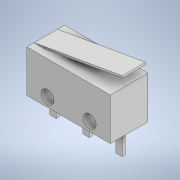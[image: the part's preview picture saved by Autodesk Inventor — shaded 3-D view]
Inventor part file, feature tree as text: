
AUTODESK INVENTOR PART (.ipt)
format: ipt  version: 2021 (Build 250183000, 183)  size: 138,752 bytes
history: native  units: mm
features: extrude x3, sketch x3
ambient origin geometry x8: Origin, YZ Plane, XZ Plane, XY Plane, X Axis, Y Axis, Z Axis, Center Point
bodies: Solid1 (feature_tree)
feature tree (6):
  extrude  "Extrusion1"  Depth=6.5mm
  extrude  "Extrusion2"  Depth=6.5mm
  extrude  "Extrusion3"  Depth=0.45mm
  sketch  "Sketch1"  dims[d0=12.85mm d1=6.5mm]
  sketch  "Sketch2"  dims[d2=1.4mm d3=6.5mm]
  sketch  "Sketch3"  dims[d4=3.25mm d5=2.0mm d6=5.8mm d7=0.0mm d9=0.3mm d10=1.745329mm d11=13.8mm d12=3.6mm d13=0.0mm d14=3.5mm d15=10.2mm d16=5.1mm d17=1.0mm d18=0.45mm d19=0.0mm]
